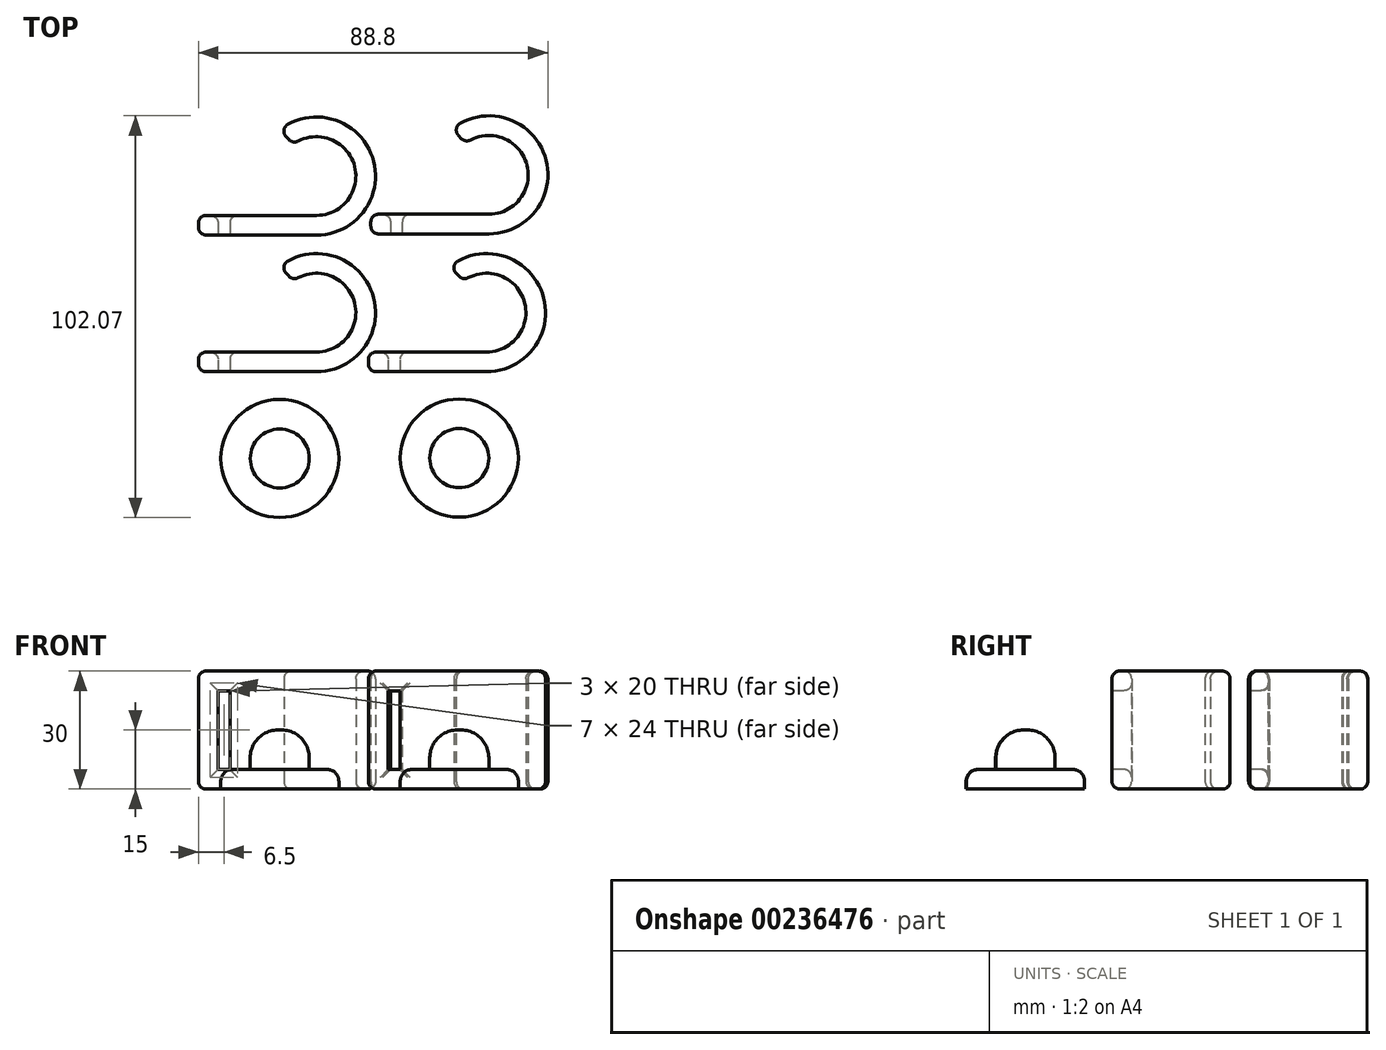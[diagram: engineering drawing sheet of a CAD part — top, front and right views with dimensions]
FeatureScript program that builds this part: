
annotation { "Feature Type Name" : "Feature", "Feature Type Description" : "" }
export const myFeature = defineFeature(function(context is Context, id is Id, definition is map)
    precondition{}
    {
        {
            var Q0;
            Q0=qCreatedBy(makeId("Top.planeOp"),FACE);
            var sketch = newSketch(context, id + "F0", { "sketchPlane" : qUnion([Q0])});
            skArc(sketch, "E0", {"start": v(0, -10) * mm, "mid": v(9.5, 3.1) * mm, "end": v(-5.9, 8.07) * mm});
            skLineSegment(sketch, "E1", {"start": v(0, -10) * mm, "end": v(-30, -10) * mm});
            skLineSegment(sketch, "E2.0", {"start": v(0, -15) * mm, "end": v(-30, -15) * mm});
            skArc(sketch, "E3.0", {"start": v(0, -15) * mm, "mid": v(14.16, 4.96) * mm, "end": v(-9.36, 11.72) * mm});
            skLineSegment(sketch, "E4", {"start": v(-5.9, 8.07) * mm, "end": v(-9.36, 11.72) * mm});
            skLineSegment(sketch, "E5", {"start": v(-30, -10) * mm, "end": v(-30, -15) * mm});
            skSolve(sketch);
        }
        {
            var Q0;
            Q0=makeQuery(id+"F0.imprint","IMPRINT",FACE,{"disambiguationData":[TD([[makeQuery(id+"F0.imprint","IMPRINT",EDGE,{"derivedFrom":sQuery(id+"F0.wireOp",EDGE,"E0")}),-1.0]])]});
            extrude(context, id + "F1", {"entities" : qUnion([Q0]), "depth" : 30 * mm, "offsetDistance" : 25 * mm});
        }
        {
            var Q0;
            Q0=makeQuery(id+"F1.opExtrude","SWEPT_FACE",FACE,{"disambiguationData":[OSD([sQuery(id+"F0.wireOp",EDGE,"E2.0")])]});
            var sketch = newSketch(context, id + "F2", { "sketchPlane" : qUnion([Q0])});
            skPoint(sketch, "E6", {"position": v(-30, 30) * mm});
            skPoint(sketch, "E7", {"position": v(-30, 0) * mm});
            skPoint(sketch, "E8", {"position": v(-25, 30) * mm});
            skPoint(sketch, "E9", {"position": v(-25, 0) * mm});
            skPoint(sketch, "E10", {"position": v(-22, 30) * mm});
            skPoint(sketch, "E11", {"position": v(-22, 0) * mm});
            skPoint(sketch, "E12", {"position": v(-30, 25) * mm});
            skPoint(sketch, "E13", {"position": v(-30, 5) * mm});
            skPoint(sketch, "E14", {"position": v(-25, 25) * mm});
            skPoint(sketch, "E15", {"position": v(-25, 5) * mm});
            skPoint(sketch, "E16", {"position": v(-22, 5) * mm});
            skPoint(sketch, "E17", {"position": v(-22, 25) * mm});
            skLineSegment(sketch, "E18", {"start": v(-25, 25) * mm, "end": v(-22, 25) * mm});
            skLineSegment(sketch, "E19", {"start": v(-22, 25) * mm, "end": v(-22, 5) * mm});
            skLineSegment(sketch, "E20", {"start": v(-22, 5) * mm, "end": v(-25, 5) * mm});
            skLineSegment(sketch, "E21", {"start": v(-25, 5) * mm, "end": v(-25, 25) * mm});
            skSolve(sketch);
        }
        {
            var Q0;
            Q0=makeQuery(id+"F2.imprint","IMPRINT",FACE,{"disambiguationData":[TD([[makeQuery(id+"F2.imprint","IMPRINT",EDGE,{"derivedFrom":sQuery(id+"F2.wireOp",EDGE,"E18")}),-1.0]])]});
            extrude(context, id + "F3", {"entities" : qUnion([Q0]), "operationType" : NewBodyOperationType.REMOVE, "oppositeDirection" : true, "depth" : 25 * mm, "offsetDistance" : 25 * mm});
        }
        {
            var Q0;
            Q0=makeQuery(id+"F1.opExtrude","CAP_FACE",FACE,{"disambiguationData":[OSD([sQuery(id+"F0.wireOp",EDGE,"E0"),sQuery(id+"F0.wireOp",EDGE,"E1"),sQuery(id+"F0.wireOp",EDGE,"E2.0"),sQuery(id+"F0.wireOp",EDGE,"E3.0"),sQuery(id+"F0.wireOp",EDGE,"E4"),sQuery(id+"F0.wireOp",EDGE,"E5")])],"isStart":false});
            var Q1;
            Q1=makeQuery(id+"F1.opExtrude","CAP_FACE",FACE,{"disambiguationData":[OSD([sQuery(id+"F0.wireOp",EDGE,"E0"),sQuery(id+"F0.wireOp",EDGE,"E1"),sQuery(id+"F0.wireOp",EDGE,"E2.0"),sQuery(id+"F0.wireOp",EDGE,"E3.0"),sQuery(id+"F0.wireOp",EDGE,"E4"),sQuery(id+"F0.wireOp",EDGE,"E5")])],"isStart":true});
            var Q2;
            Q2=makeQuery(id+"F1.opExtrude","SWEPT_FACE",FACE,{"disambiguationData":[OSD([sQuery(id+"F0.wireOp",EDGE,"E5")])]});
            var Q3;
            Q3=makeQuery(id+"F1.opExtrude","SWEPT_FACE",FACE,{"disambiguationData":[OSD([sQuery(id+"F0.wireOp",EDGE,"E4")])]});
            var Q4;
            Q4=makeQuery(id+"F3.boolean.opBoolean","COPY",EDGE,{"derivedFrom":makeQuery(id+"F3.opExtrude","CAP_EDGE",EDGE,{"disambiguationData":[OSD([sQuery(id+"F2.wireOp",EDGE,"E19")])],"isStart":true})});
            var Q5;
            Q5=makeQuery(id+"F3.boolean.opBoolean","COPY",EDGE,{"derivedFrom":makeQuery(id+"F3.opExtrude","CAP_EDGE",EDGE,{"disambiguationData":[OSD([sQuery(id+"F2.wireOp",EDGE,"E21")])],"isStart":true})});
            var Q6;
            Q6=makeQuery(id+"F3.boolean.opBoolean","COPY",EDGE,{"derivedFrom":makeQuery(id+"F3.opExtrude","CAP_EDGE",EDGE,{"disambiguationData":[OSD([sQuery(id+"F2.wireOp",EDGE,"E20")])],"isStart":true})});
            var Q7;
            Q7=makeQuery(id+"F3.boolean.opBoolean","COPY",EDGE,{"derivedFrom":makeQuery(id+"F3.opExtrude","CAP_EDGE",EDGE,{"disambiguationData":[OSD([sQuery(id+"F2.wireOp",EDGE,"E18")])],"isStart":true})});
            var Q8;
            Q8=makeQuery(id+"F1.opExtrude","SWEPT_FACE",FACE,{"disambiguationData":[OSD([sQuery(id+"F0.wireOp",EDGE,"E1")])]});
            fillet(context, id + "F4", {"entities" : qUnion([Q0, Q1, Q2, Q3, Q4, Q5, Q6, Q7, Q8]), "tangentPropagation" : true, "radius" : 2 * mm, "defaultsChanged" : false, "vertexSettings" : [], "allowEdgeOverflow" : false});
        }
        {
            var Q0;
            Q0=makeQuery(id+"F1.opExtrude","SWEPT_BODY",BODY,{"disambiguationData":[OSD([sQuery(id+"F0.wireOp",EDGE,"E0"),sQuery(id+"F0.wireOp",EDGE,"E1"),sQuery(id+"F0.wireOp",EDGE,"E2.0"),sQuery(id+"F0.wireOp",EDGE,"E3.0"),sQuery(id+"F0.wireOp",EDGE,"E4"),sQuery(id+"F0.wireOp",EDGE,"E5")])]});
            transform(context, id + "F5", {"entities" : qUnion([Q0]), "transformType" : TransformType.TRANSLATION_3D, "dx" : 0 * mm, "dy" : 34.7 * mm, "dz" : 0 * mm, "makeCopy" : true});
        }
        {
            var Q0;
            Q0=makeQuery(id+"F1.opExtrude","SWEPT_BODY",BODY,{"disambiguationData":[OSD([sQuery(id+"F0.wireOp",EDGE,"E0"),sQuery(id+"F0.wireOp",EDGE,"E1"),sQuery(id+"F0.wireOp",EDGE,"E2.0"),sQuery(id+"F0.wireOp",EDGE,"E3.0"),sQuery(id+"F0.wireOp",EDGE,"E4"),sQuery(id+"F0.wireOp",EDGE,"E5")])]});
            transform(context, id + "F6", {"entities" : qUnion([Q0]), "transformType" : TransformType.TRANSLATION_3D, "dx" : 43.2 * mm, "dy" : 0 * mm, "dz" : 0 * mm, "makeCopy" : true});
        }
        {
            var Q0;
            Q0=makeQuery(id+"F6.opPattern","COPY",BODY,{"derivedFrom":makeQuery(id+"F1.opExtrude","SWEPT_BODY",BODY,{"disambiguationData":[OSD([sQuery(id+"F0.wireOp",EDGE,"E0"),sQuery(id+"F0.wireOp",EDGE,"E1"),sQuery(id+"F0.wireOp",EDGE,"E2.0"),sQuery(id+"F0.wireOp",EDGE,"E3.0"),sQuery(id+"F0.wireOp",EDGE,"E4"),sQuery(id+"F0.wireOp",EDGE,"E5")])]}),"instanceName":"1"});
            transform(context, id + "F7", {"entities" : qUnion([Q0]), "transformType" : TransformType.TRANSLATION_3D, "dx" : 0.6 * mm, "dy" : 35 * mm, "dz" : 0 * mm, "makeCopy" : true});
        }
        {
            var Q0;
            Q0=qCreatedBy(makeId("Top.planeOp"),FACE);
            var sketch = newSketch(context, id + "F8", { "sketchPlane" : qUnion([Q0])});
            skCircle(sketch, "E22", {"center": v(36.28, -36.97) * mm, "radius": 7.5 * mm});
            skCircle(sketch, "E23", {"center": v(36.28, -36.97) * mm, "radius": 15 * mm});
            skSolve(sketch);
        }
        {
            var Q0;
            Q0=makeQuery(id+"F8.imprint","IMPRINT",FACE,{"disambiguationData":[TD([[makeQuery(id+"F8.imprint","IMPRINT",EDGE,{"derivedFrom":sQuery(id+"F8.wireOp",EDGE,"E22")}),1.0]])]});
            extrude(context, id + "F9", {"entities" : qUnion([Q0]), "depth" : 15 * mm, "offsetDistance" : 25 * mm});
        }
        {
            var Q0;
            Q0=makeQuery(id+"F9.opExtrude","CAP_FACE",FACE,{"disambiguationData":[OSD([sQuery(id+"F8.wireOp",EDGE,"E22")])],"isStart":false});
            fillet(context, id + "F10", {"entities" : qUnion([Q0]), "tangentPropagation" : true, "radius" : 7 * mm, "defaultsChanged" : true, "vertexSettings" : [], "allowEdgeOverflow" : false});
        }
        {
            var Q0;
            Q0 = qSketchRegion(id + "F8", true);
            extrude(context, id + "F11", {"entities" : qUnion([Q0]), "operationType" : NewBodyOperationType.ADD, "depth" : 5 * mm, "offsetDistance" : 25 * mm});
        }
        {
            var Q0;
            Q0=makeQuery(id+"F11.opExtrude","CAP_EDGE",EDGE,{"disambiguationData":[OSD([sQuery(id+"F8.wireOp",EDGE,"E23")])],"isStart":false});
            var Q1;
            Q1=makeQuery(id+"F11.opExtrude","CAP_EDGE",EDGE,{"disambiguationData":[OSD([sQuery(id+"F8.wireOp",EDGE,"E22")])],"isStart":false});
            fillet(context, id + "F12", {"entities" : qUnion([Q0, Q1]), "tangentPropagation" : true, "radius" : 3 * mm, "defaultsChanged" : true, "vertexSettings" : [], "allowEdgeOverflow" : false});
        }
        {
            var Q0;
            Q0=makeQuery(id+"F9.opExtrude","SWEPT_BODY",BODY,{"disambiguationData":[OSD([sQuery(id+"F8.wireOp",EDGE,"E22")])]});
            transform(context, id + "F13", {"entities" : qUnion([Q0]), "transformType" : TransformType.TRANSLATION_3D, "dx" : -45.6 * mm, "dy" : -0.1 * mm, "dz" : 0 * mm, "makeCopy" : true});
        }
    });
